# Revit family: LAMP_FIL 70 TECH SUSPENDED DALI
name_source: partatom
category: Luminarias
revit_build: Autodesk Revit 2015 (Build: 20140606_1530(x64)
units: mm (PartAtom-declared; Revit-internal decimal feet)

## types (16) — shared parameters
CRI = 80
Cambio de temperatura de color de luz atenuada = <Ninguno>
Comentarios de tipo = Availability of switching between accessories through visibility parameters when placed in a project.
Fabricante = LAMP
Filtro de color = 16777215
Gear = Adjustable DALI
IEE = A+
IFC Clasificación = Light Fixture
Installation instructions = https://www.lamp.es
Insulation class = I
LED Lifetime = 50.000 L80 B10
Last update = 17/08/2020
Luminaire type = Indoor - Modular System
Lámpara = MID-POWER LED
MacAdam = 3
Manufacturer URL = http://www.lamp.es
Manufacturer country = Spain
Manufacturer name = LAMP
Material Reflector = LAMP_PC Reflector Fil Tech Metalizado
Model explanation = Availability of switching between accessories through visibility parameters when placed in a project.
Product URL = https://www.lamp.es
Product datasheet = https://www.lamp.es
Protection rating = IP20
Type = MID POWER NICHIA
UGR = 19
Ángulo de inclinación = 90,00°

## per-type parameters (varying)
| type | Archivo de red fotométrica | Descripción | Dimensions | Efficacy | Finish | Largo | Longitud de línea de emisión | Material Perfil | Modelo | Plum | Power | Power Supply | Product code | UniClass 1.4 Code | UniClass 2.0 Code | Weight |
| 1000MM 1600LM 3000K GREY | 4741103.IES | FIL 70 TECH SUS 1M 1600 WW DALI GR. | 1000 x 70 x 70 mm | 106 lm/W | Gloss grey | 1000 mm  [stored 3.28084 ft] | 1000 mm  [stored 3.28084 ft] | LAMP_Aluminio Perfil Fil GR | F71SF100LOTS830DG | 15 W | 12 W | 230V-50Hz | F71SF100LOTS830DG | F71SF100LOTS830DG | F71SF100LOTS830DG | 1,95 kg |
| 1000MM 1600LM 3000K WHITE | 4741100.IES | FIL 70 TECH SUS 1M 1600 WW DALI WH. | 1000 x 70 x 70 mm | 106 lm/W | Matt white | 1000 mm  [stored 3.28084 ft] | 1000 mm  [stored 3.28084 ft] | LAMP_Aluminio Perfil Fil BL | F71SF100LOTS830DW | 15 W | 12 W | 230V-50Hz | F71SF100LOTS830DW | F71SF100LOTS830DW | F71SF100LOTS830DW | 1,95 kg |
| 1000MM 1600LM 4000K WHITE | 4740100.IES | FIL 70 TECH SUS 1M 1600 NW DALI WH. | 1000 x 70 x 70 mm | 106 lm/W | Matt white | 1000 mm  [stored 3.28084 ft] | 1000 mm  [stored 3.28084 ft] | LAMP_Aluminio Perfil Fil BL | F71SF100LOTS840DW | 15 W | 12 W | 220-240V 50-60Hz | F71SF100LOTS840DW | F71SF100LOTS840DW | F71SF100LOTS840DW | 1,95 kg |
| 1000MM 1600LM 4000K GREY | 4740103.IES | FIL 70 TECH SUS 1M 1600 NW DALI GR. | 1000 x 70 x 70 mm | 106 lm/W | Gloss grey | 1000 mm  [stored 3.28084 ft] | 1000 mm  [stored 3.28084 ft] | LAMP_Aluminio Perfil Fil GR | F71SF100LOTS840DG | 15 W | 12 W | 220-240V 50-60Hz | F71SF100LOTS840DG | F71SF100LOTS840DG | F71SF100LOTS840DG | 1,95 kg |
| 1000MM 3200LM 3000K WHITE | 4741110.IES | FIL 70 TECH SUS 1M 3200 WW DALI WH. | 1000 x 70 x 70 mm | 102 lm/W | Matt white | 1000 mm  [stored 3.28084 ft] | 1000 mm  [stored 3.28084 ft] | LAMP_Aluminio Perfil Fil BL | F71SF100MOTS830DW | 24 W | 21 W | 230V-50Hz | F71SF100MOTS830DW | F71SF100MOTS830DW | F71SF100MOTS830DW | 2,00 kg |
| 1000MM 3200LM 3000K GREY | 4741113.IES | FIL 70 TECH SUS 1M 3200 WW DALI GR. | 1000 x 70 x 70 mm | 102 lm/W | Gloss grey | 1000 mm  [stored 3.28084 ft] | 1000 mm  [stored 3.28084 ft] | LAMP_Aluminio Perfil Fil GR | F71SF100MOTS830DG | 24 W | 21 W | 230V-50Hz | F71SF100MOTS830DG | F71SF100MOTS830DG | F71SF100MOTS830DG | 2,00 kg |
| 1000MM 3200LM 4000K WHITE | 4740110.IES | FIL 70 TECH SUS 1M 3200 NW DALI WH. | 1000 x 70 x 70 mm | 102 lm/W | Matt white | 1000 mm  [stored 3.28084 ft] | 1000 mm  [stored 3.28084 ft] | LAMP_Aluminio Perfil Fil BL | F71SF100MOTS840DW | 24 W | 21 W | 220-240V 50-60Hz | F71SF100MOTS840DW | F71SF100MOTS840DW | F71SF100MOTS840DW | 2,00 kg |
| 1000MM 3200LM 4000K GREY | 4740113.IES | FIL 70 TECH SUS 1M 3200 NW DALI GR. | 1000 x 70 x 70 mm | 102 lm/W | Gloss grey | 1000 mm  [stored 3.28084 ft] | 1000 mm  [stored 3.28084 ft] | LAMP_Aluminio Perfil Fil GR | F71SF100MOTS840DG | 24 W | 21 W | 220-240V 50-60Hz | F71SF100MOTS840DG | F71SF100MOTS840DG | F71SF100MOTS840DG | 2,00 kg |
| 2000MM 3200LM 3000K WHITE | 4741200.IES | FIL 70 TECH SUS 2M 3200 WW DALI WH. | 2000 x 70 x 70 mm | 114 lm/W | Matt white | 2000 mm  [stored 6.56168 ft] | 2000 mm  [stored 6.56168 ft] | LAMP_Aluminio Perfil Fil BL | F71SF200MOTS830DW | 27 W | 25 W | 230V-50Hz | F71SF200MOTS830DW | F71SF200MOTS830DW | F71SF200MOTS830DW | 3,38 kg |
| 2000MM 3200LM 3000K GREY | 4741203.IES | FIL 70 TECH SUS 2M 3200 WW DALI GR. | 2000 x 70 x 70 mm | 114 lm/W | Gloss grey | 2000 mm  [stored 6.56168 ft] | 2000 mm  [stored 6.56168 ft] | LAMP_Aluminio Perfil Fil GR | F71SF200MOTS830DG | 27 W | 25 W | 230V-50Hz | F71SF200MOTS830DG | F71SF200MOTS830DG | F71SF200MOTS830DG | 3,38 kg |
| 2000MM 3200LM 4000K WHITE | 4740200.IES | FIL 70 TECH SUS 2M 3200 NW DALI WH. | 2000 x 70 x 70 mm | 114 lm/W | Matt white | 2000 mm  [stored 6.56168 ft] | 2000 mm  [stored 6.56168 ft] | LAMP_Aluminio Perfil Fil BL | F71SF200MOTS840DW | 27 W | 25 W | 220-240V 50-60Hz | F71SF200MOTS840DW | F71SF200MOTS840DW | F71SF200MOTS840DW | 3,38 kg |
| 2000MM 3200LM 4000K GREY | 4740203.IES | FIL 70 TECH SUS 2M 3200 NW DALI GR. | 2000 x 70 x 70 mm | 114 lm/W | Gloss grey | 2000 mm  [stored 6.56168 ft] | 2000 mm  [stored 6.56168 ft] | LAMP_Aluminio Perfil Fil GR | F71SF200MOTS840DG | 27 W | 25 W | 220-240V 50-60Hz | F71SF200MOTS840DG | F71SF200MOTS840DG | F71SF200MOTS840DG | 3,38 kg |
| 2000MM 6400LM 3000K WHITE | 4741210.IES | FIL 70 TECH SUS 2M 6400 WW DALI WH. | 2000 x 70 x 70 mm | 129 lm/W | Matt white | 2000 mm  [stored 6.56168 ft] | 2000 mm  [stored 6.56168 ft] | LAMP_Aluminio Perfil Fil BL | F71SF200HOTS830DW | 45 W | 42 W | 230V-50Hz | F71SF200HOTS830DW | F71SF200HOTS830DW | F71SF200HOTS830DW | 3,90 kg |
| 2000MM 6400LM 3000K GREY | 4741213.IES | FIL 70 TECH SUS 2M 6400 WW DALI GR. | 2000 x 70 x 70 mm | 107 lm/W | Gloss grey | 2000 mm  [stored 6.56168 ft] | 2000 mm  [stored 6.56168 ft] | LAMP_Aluminio Perfil Fil GR | F71SF200HOTS830DG | 45 W | 42 W | 230V-50Hz | F71SF200HOTS830DG | F71SF200HOTS830DG | F71SF200HOTS830DG | 3,90 kg |
| 2000MM 6400LM 4000K WHITE | 4740210.IES | FIL 70 TECH SUS 2M 6400 NW DALI WH. | 2000 x 70 x 70 mm | 107 lm/W | Matt white | 2000 mm  [stored 6.56168 ft] | 2000 mm  [stored 6.56168 ft] | LAMP_Aluminio Perfil Fil BL | F71SF200HOTS840DW | 45 W | 42 W | 220-240V 50-60Hz | F71SF200HOTS840DW | F71SF200HOTS840DW | F71SF200HOTS840DW | 3,90 kg |
| 2000MM 6400LM 4000K GREY | 4740213.IES | FIL 70 TECH SUS 2M 6400 NW DALI GR. | 2000 x 70 x 70 mm | 107 lm/W | Gloss grey | 2000 mm  [stored 6.56168 ft] | 2000 mm  [stored 6.56168 ft] | LAMP_Aluminio Perfil Fil GR | F71SF200HOTS840DG | 45 W | 42 W | 220-240V 50-60Hz | F71SF200HOTS840DG | F71SF200HOTS840DG | F71SF200HOTS840DG | 3,90 kg |

note: [stored X ft] marks values corroborated as IEEE doubles in the binary element streams (Revit-internal decimal feet)

## geometry (parser evidence)
native form markers: Blend x6
no freeform markers — native parametric forms only
